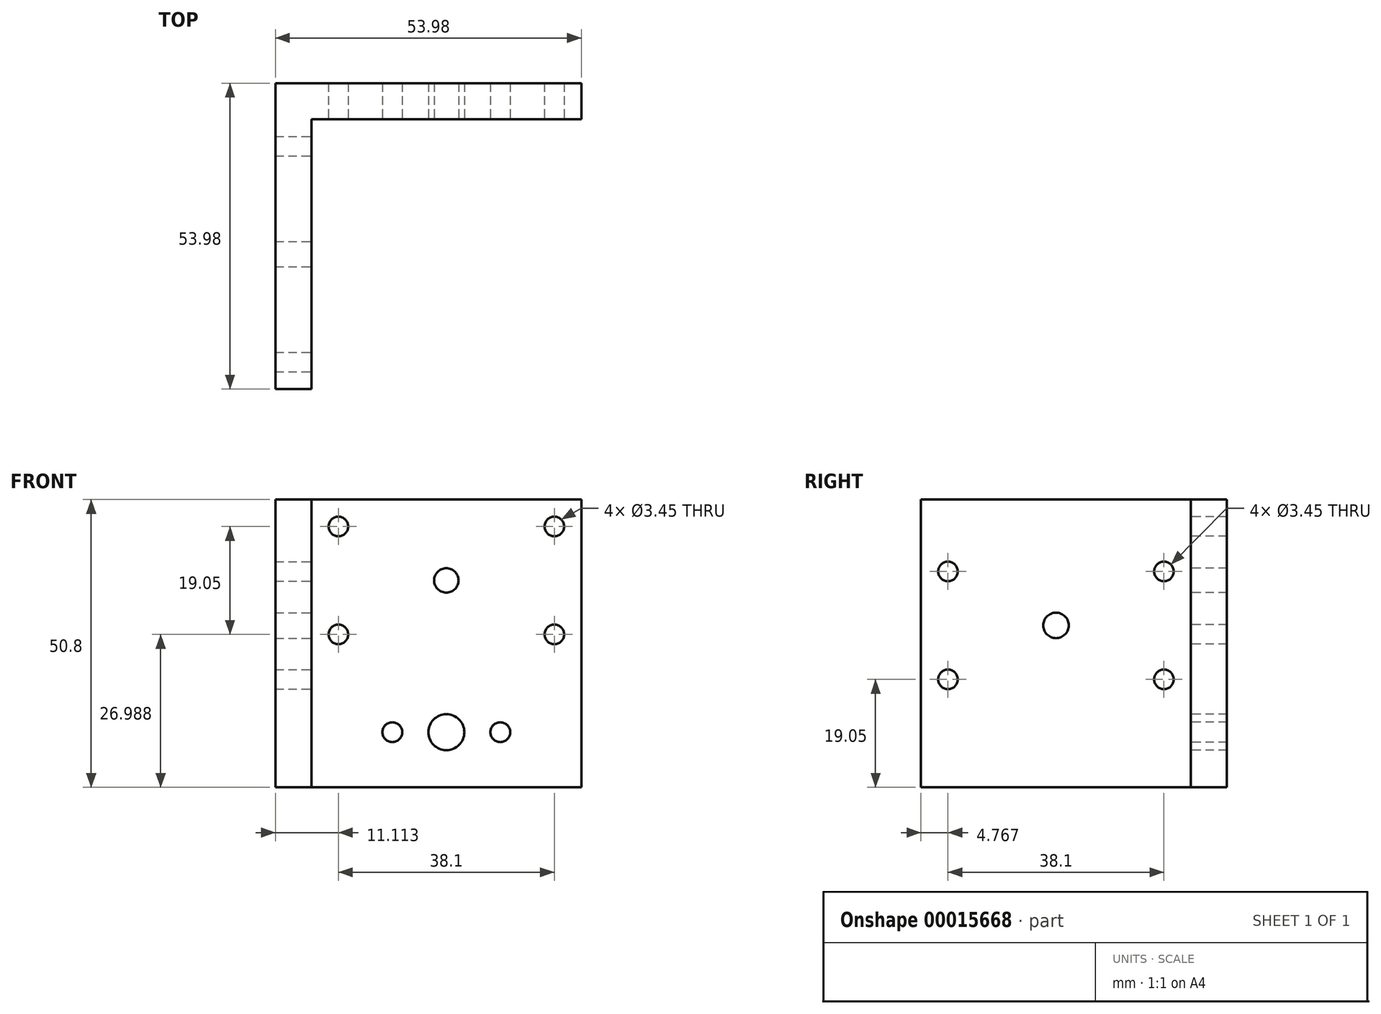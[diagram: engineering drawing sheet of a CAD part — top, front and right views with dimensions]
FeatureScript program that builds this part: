
annotation { "Feature Type Name" : "Feature", "Feature Type Description" : "" }
export const myFeature = defineFeature(function(context is Context, id is Id, definition is map)
    precondition{}
    {
        {
            var Q0;
            Q0=qCreatedBy(makeId("Top.planeOp"),FACE);
            var sketch = newSketch(context, id + "F0", { "sketchPlane" : qUnion([Q0])});
            skLineSegment(sketch, "E0.bottom", {"start": v(0, 0) * mm, "end": v(53.98, 0) * mm});
            skLineSegment(sketch, "E0.left", {"start": v(0, 0) * mm, "end": v(0, -53.98) * mm});
            skLineSegment(sketch, "E1.top", {"start": v(53.98, -6.35) * mm, "end": v(6.35, -6.35) * mm});
            skLineSegment(sketch, "E1.right", {"start": v(6.35, -53.98) * mm, "end": v(6.35, -6.35) * mm});
            skLineSegment(sketch, "E2", {"start": v(0, -53.98) * mm, "end": v(6.35, -53.98) * mm});
            skLineSegment(sketch, "E3", {"start": v(53.98, -6.35) * mm, "end": v(53.98, 0) * mm});
            skSolve(sketch);
        }
        {
            var Q0;
            Q0=qSketchRegion(id+"F0",true);
            extrude(context, id + "F1", {"entities" : qUnion([Q0]), "depth" : 50.8 * mm});
        }
        {
            var Q0;
            Q0=makeQuery(id+"F1.opExtrude","SWEPT_FACE",FACE,{"disambiguationData":[OSD([sQuery(id+"F0.wireOp",EDGE,"E1.right")])]});
            var sketch = newSketch(context, id + "F2", { "sketchPlane" : qUnion([Q0])});
            skLineSegment(sketch, "E4.bottom", {"start": v(-49.21, 38.1) * mm, "end": v(-11.11, 38.1) * mm, "construction": true});
            skLineSegment(sketch, "E4.top", {"start": v(-49.21, 19.05) * mm, "end": v(-11.11, 19.05) * mm, "construction": true});
            skLineSegment(sketch, "E4.left", {"start": v(-49.21, 38.1) * mm, "end": v(-49.21, 19.05) * mm, "construction": true});
            skLineSegment(sketch, "E4.right", {"start": v(-11.11, 38.1) * mm, "end": v(-11.11, 19.05) * mm, "construction": true});
            skPoint(sketch, "E4.middle", {"position": v(-30.16, 28.58) * mm});
            skLineSegment(sketch, "E5.bottom", {"start": v(-49.21, 38.1) * mm, "end": v(-53.98, 38.1) * mm, "construction": true});
            skLineSegment(sketch, "E5.top", {"start": v(-49.21, 50.8) * mm, "end": v(-53.98, 50.8) * mm, "construction": true});
            skLineSegment(sketch, "E5.left", {"start": v(-49.21, 38.1) * mm, "end": v(-49.21, 50.8) * mm, "construction": true});
            skLineSegment(sketch, "E5.right", {"start": v(-53.98, 38.1) * mm, "end": v(-53.98, 50.8) * mm, "construction": true});
            skCircle(sketch, "E6", {"center": v(-11.11, 38.1) * mm, "radius": 1.73 * mm});
            skCircle(sketch, "E7", {"center": v(-11.11, 19.05) * mm, "radius": 1.73 * mm});
            skCircle(sketch, "E8", {"center": v(-49.21, 38.1) * mm, "radius": 1.73 * mm});
            skCircle(sketch, "E9", {"center": v(-30.16, 28.58) * mm, "radius": 2.25 * mm});
            skCircle(sketch, "E10", {"center": v(-49.21, 19.05) * mm, "radius": 1.73 * mm});
            skSolve(sketch);
        }
        {
            var Q0;
            Q0=qSketchRegion(id+"F2",true);
            var Q1;
            Q1=makeQuery(id+"F1.opExtrude","SWEPT_FACE",FACE,{"disambiguationData":[OSD([sQuery(id+"F0.wireOp",EDGE,"E0.left")])]});
            extrude(context, id + "F3", {"entities" : qUnion([Q0]), "operationType" : NewBodyOperationType.REMOVE, "endBound" : BoundingType.UP_TO_SURFACE, "oppositeDirection" : true, "endBoundEntityFace" : qUnion([Q1]), "depth" : 25.4 * mm});
        }
        {
            var Q0;
            Q0=makeQuery(id+"F1.opExtrude","SWEPT_FACE",FACE,{"disambiguationData":[OSD([sQuery(id+"F0.wireOp",EDGE,"E1.top")])]});
            var sketch = newSketch(context, id + "F4", { "sketchPlane" : qUnion([Q0])});
            skLineSegment(sketch, "E11.bottom", {"start": v(49.21, 26.99) * mm, "end": v(11.11, 26.99) * mm, "construction": true});
            skLineSegment(sketch, "E11.top", {"start": v(49.21, 46.04) * mm, "end": v(11.11, 46.04) * mm, "construction": true});
            skLineSegment(sketch, "E11.left", {"start": v(49.21, 26.99) * mm, "end": v(49.21, 46.04) * mm, "construction": true});
            skLineSegment(sketch, "E11.right", {"start": v(11.11, 26.99) * mm, "end": v(11.11, 46.04) * mm, "construction": true});
            skPoint(sketch, "E11.middle", {"position": v(30.16, 36.51) * mm});
            skLineSegment(sketch, "E12.bottom", {"start": v(49.21, 46.04) * mm, "end": v(53.98, 46.04) * mm, "construction": true});
            skLineSegment(sketch, "E12.top", {"start": v(49.21, 50.8) * mm, "end": v(53.98, 50.8) * mm, "construction": true});
            skLineSegment(sketch, "E12.left", {"start": v(49.21, 50.8) * mm, "end": v(49.21, 46.04) * mm, "construction": true});
            skLineSegment(sketch, "E12.right", {"start": v(53.98, 50.8) * mm, "end": v(53.98, 46.04) * mm, "construction": true});
            skCircle(sketch, "E13", {"center": v(30.16, 36.51) * mm, "radius": 2.15 * mm});
            skCircle(sketch, "E14", {"center": v(49.21, 46.04) * mm, "radius": 1.73 * mm});
            skCircle(sketch, "E15", {"center": v(49.21, 26.99) * mm, "radius": 1.73 * mm});
            skCircle(sketch, "E16", {"center": v(11.11, 26.99) * mm, "radius": 1.73 * mm});
            skCircle(sketch, "E17", {"center": v(11.11, 46.04) * mm, "radius": 1.73 * mm});
            skLineSegment(sketch, "E18", {"start": v(30.16, 26.99) * mm, "end": v(30.16, 22.22) * mm, "construction": true});
            skLineSegment(sketch, "E19", {"start": v(30.16, 22.22) * mm, "end": v(30.16, 9.72) * mm, "construction": true});
            skCircle(sketch, "E20", {"center": v(30.16, 9.72) * mm, "radius": 12.5 * mm, "construction": true});
            skLineSegment(sketch, "E21", {"start": v(20.64, 9.72) * mm, "end": v(39.69, 9.72) * mm, "construction": true});
            skCircle(sketch, "E22", {"center": v(20.64, 9.72) * mm, "radius": 1.75 * mm});
            skCircle(sketch, "E23", {"center": v(39.69, 9.72) * mm, "radius": 1.75 * mm});
            skCircle(sketch, "E24", {"center": v(30.16, 9.72) * mm, "radius": 3.18 * mm});
            skSolve(sketch);
        }
        {
            var Q0;
            Q0=qSketchRegion(id+"F4",true);
            var Q1;
            Q1=makeQuery(id+"F1.opExtrude","SWEPT_FACE",FACE,{"disambiguationData":[OSD([sQuery(id+"F0.wireOp",EDGE,"E0.bottom")])]});
            extrude(context, id + "F5", {"entities" : qUnion([Q0]), "operationType" : NewBodyOperationType.REMOVE, "endBound" : BoundingType.UP_TO_SURFACE, "oppositeDirection" : true, "endBoundEntityFace" : qUnion([Q1]), "depth" : 25.4 * mm});
        }
    });
